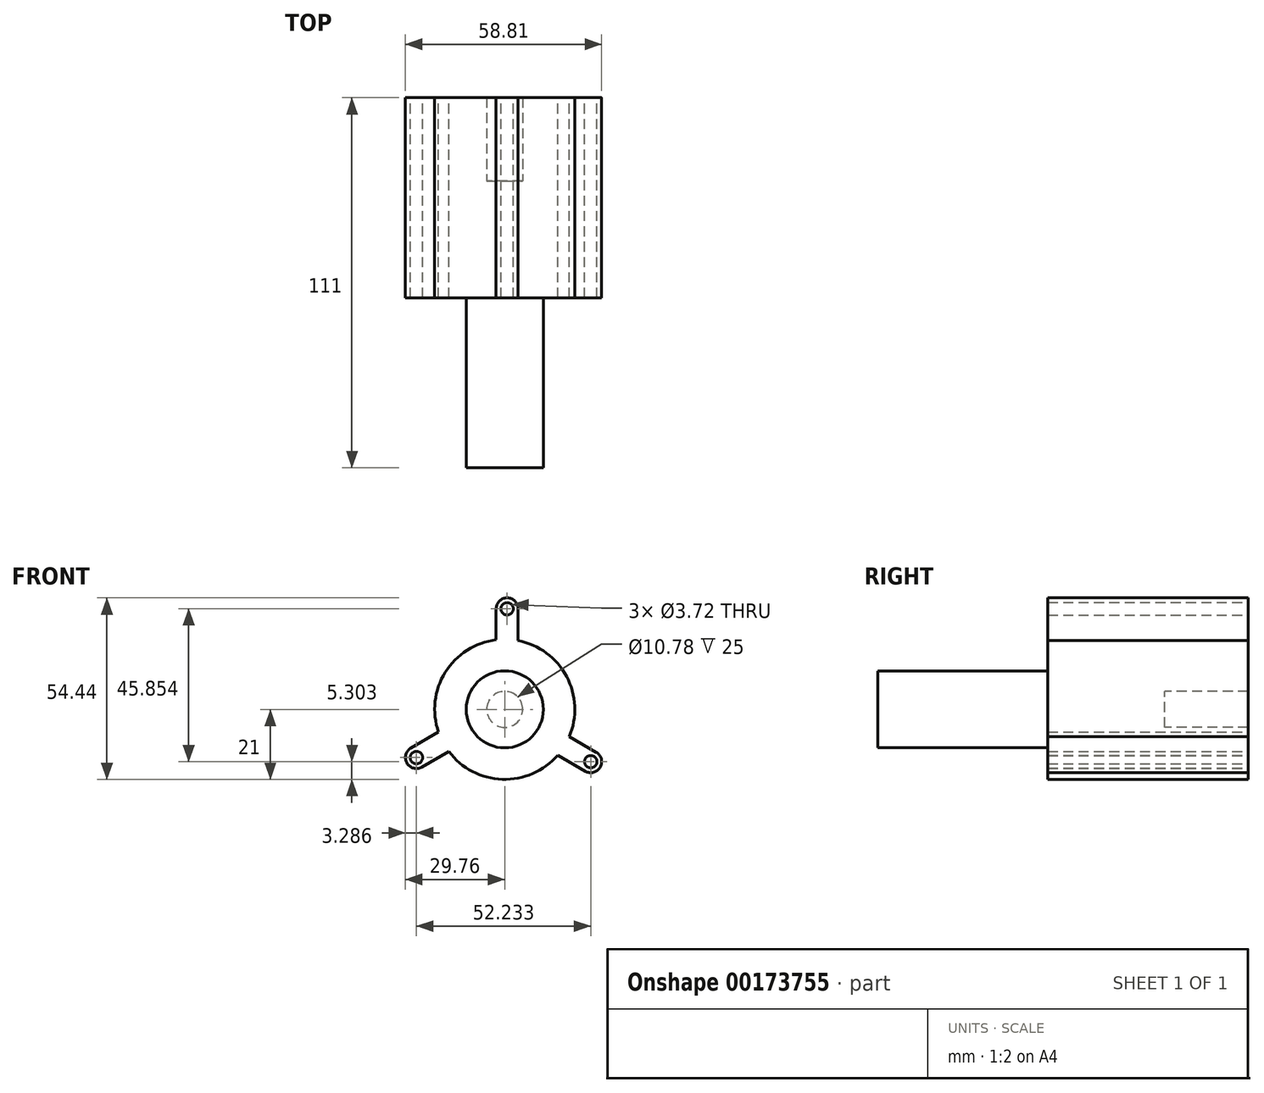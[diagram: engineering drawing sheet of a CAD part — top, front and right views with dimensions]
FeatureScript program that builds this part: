
annotation { "Feature Type Name" : "Feature", "Feature Type Description" : "" }
export const myFeature = defineFeature(function(context is Context, id is Id, definition is map)
    precondition{}
    {
        {
            var Q0;
            Q0=qCreatedBy(makeId("Front.planeOp"),FACE);
            var sketch = newSketch(context, id + "F0", { "sketchPlane" : qUnion([Q0])});
            skCircle(sketch, "E0", {"center": v(0, 0) * mm, "radius": 21 * mm});
            skLineSegment(sketch, "E1.left", {"start": v(-2.57, 30.16) * mm, "end": v(-2.57, 15) * mm});
            skLineSegment(sketch, "E1.right", {"start": v(4, 30.16) * mm, "end": v(4, 15) * mm});
            skArc(sketch, "E2", {"start": v(4, 30.16) * mm, "mid": v(0.71, 33.44) * mm, "end": v(-2.57, 30.16) * mm});
            skCircle(sketch, "E3", {"center": v(0.71, 30.16) * mm, "radius": 1.86 * mm});
            skLineSegment(sketch, "E4.1.0", {"start": v(24.12, -18.54) * mm, "end": v(11, -10.97) * mm});
            skLineSegment(sketch, "E4.1.1", {"start": v(27.4, -12.85) * mm, "end": v(14.28, -5.28) * mm});
            skArc(sketch, "E4.1.2", {"start": v(24.12, -18.54) * mm, "mid": v(28.6, -17.34) * mm, "end": v(27.4, -12.85) * mm});
            skCircle(sketch, "E4.1.3", {"center": v(25.76, -15.7) * mm, "radius": 1.86 * mm});
            skLineSegment(sketch, "E4.2.0", {"start": v(-28.12, -11.61) * mm, "end": v(-15, -4.04) * mm});
            skLineSegment(sketch, "E4.2.1", {"start": v(-24.83, -17.3) * mm, "end": v(-11.7, -9.73) * mm});
            skArc(sketch, "E4.2.2", {"start": v(-28.12, -11.61) * mm, "mid": v(-29.32, -16.1) * mm, "end": v(-24.83, -17.3) * mm});
            skCircle(sketch, "E4.2.3", {"center": v(-26.47, -14.46) * mm, "radius": 1.86 * mm});
            skLineSegment(sketch, "E4.anchor1", {"start": v(0, 0) * mm, "end": v(4, 15) * mm, "construction": true});
            skLineSegment(sketch, "E4.anchor2", {"start": v(0, 0) * mm, "end": v(-15, -4.04) * mm, "construction": true});
            skSolve(sketch);
        }
        {
            var Q0;
            {var subQ0=sQuery(id+"F0.wireOp",EDGE,"E0");var subQ4=makeQuery(id+"F0.imprint","INTERSECT",VERTEX,{"derivedFrom":[subQ0,sQuery(id+"F0.wireOp",EDGE,"E1.left")]});Q0=makeQuery(id+"F0.imprint","IMPRINT",FACE,{"disambiguationData":[TD([[makeQuery(id+"F0.imprint","IMPRINT",EDGE,{"disambiguationData":[TD([[subQ4,1.0]])],"derivedFrom":subQ0}),1.0]])]});}
            var Q1;
            {var subQ0=sQuery(id+"F0.wireOp",EDGE,"E2");Q1=makeQuery(id+"F0.imprint","IMPRINT",FACE,{"disambiguationData":[TD([[makeQuery(id+"F0.imprint","IMPRINT",EDGE,{"derivedFrom":subQ0}),1.0]])]});}
            var Q2;
            {var subQ0=sQuery(id+"F0.wireOp",EDGE,"E2");Q2=makeQuery(id+"F0.imprint","IMPRINT",FACE,{"disambiguationData":[TD([[makeQuery(id+"F0.imprint","IMPRINT",EDGE,{"derivedFrom":subQ0}),1.0]])]});}
            var Q3;
            {var subQ0=sQuery(id+"F0.wireOp",EDGE,"E4.2.2");Q3=makeQuery(id+"F0.imprint","IMPRINT",FACE,{"disambiguationData":[TD([[makeQuery(id+"F0.imprint","IMPRINT",EDGE,{"derivedFrom":subQ0}),1.0]])]});}
            var Q4;
            {var subQ0=sQuery(id+"F0.wireOp",EDGE,"E4.1.2");Q4=makeQuery(id+"F0.imprint","IMPRINT",FACE,{"disambiguationData":[TD([[makeQuery(id+"F0.imprint","IMPRINT",EDGE,{"derivedFrom":subQ0}),1.0]])]});}
            extrude(context, id + "F1", {"entities" : qUnion([Q0, Q1, Q2, Q3, Q4]), "depth" : 25 * mm});
        }
        {
            var Q0;
            Q0=makeQuery(id+"F1.opExtrude","CAP_FACE",FACE,{"disambiguationData":[OSD([sQuery(id+"F0.wireOp",EDGE,"E0"),sQuery(id+"F0.wireOp",EDGE,"E1.left"),sQuery(id+"F0.wireOp",EDGE,"E1.right"),sQuery(id+"F0.wireOp",EDGE,"E2"),sQuery(id+"F0.wireOp",EDGE,"E3"),sQuery(id+"F0.wireOp",EDGE,"E4.1.0"),sQuery(id+"F0.wireOp",EDGE,"E4.1.1"),sQuery(id+"F0.wireOp",EDGE,"E4.1.2"),sQuery(id+"F0.wireOp",EDGE,"E4.1.3"),sQuery(id+"F0.wireOp",EDGE,"E4.2.0"),sQuery(id+"F0.wireOp",EDGE,"E4.2.1"),sQuery(id+"F0.wireOp",EDGE,"E4.2.2"),sQuery(id+"F0.wireOp",EDGE,"E4.2.3")])],"isStart":true});
            var Q1;
            Q1=makeQuery(id+"F1.opExtrude","CAP_FACE",FACE,{"disambiguationData":[OSD([sQuery(id+"F0.wireOp",EDGE,"E0"),sQuery(id+"F0.wireOp",EDGE,"E1.left"),sQuery(id+"F0.wireOp",EDGE,"E1.right"),sQuery(id+"F0.wireOp",EDGE,"E2"),sQuery(id+"F0.wireOp",EDGE,"E3"),sQuery(id+"F0.wireOp",EDGE,"E4.1.0"),sQuery(id+"F0.wireOp",EDGE,"E4.1.1"),sQuery(id+"F0.wireOp",EDGE,"E4.1.2"),sQuery(id+"F0.wireOp",EDGE,"E4.1.3"),sQuery(id+"F0.wireOp",EDGE,"E4.2.0"),sQuery(id+"F0.wireOp",EDGE,"E4.2.1"),sQuery(id+"F0.wireOp",EDGE,"E4.2.2"),sQuery(id+"F0.wireOp",EDGE,"E4.2.3")])],"isStart":false});
            extrude(context, id + "F2", {"entities" : qUnion([Q0, Q1]), "operationType" : NewBodyOperationType.ADD, "depth" : 25 * mm});
        }
        {
            var Q0;
            Q0=qCreatedBy(makeId("Front.planeOp"),FACE);
            var sketch = newSketch(context, id + "F3", { "sketchPlane" : qUnion([Q0])});
            skCircle(sketch, "E5", {"center": v(0, 0) * mm, "radius": 11.54 * mm});
            skSolve(sketch);
        }
        {
            var Q0;
            Q0 = qSketchRegion(id + "F3", true);
            extrude(context, id + "F4", {"entities" : qUnion([Q0]), "operationType" : NewBodyOperationType.ADD, "depth" : 80 * mm});
        }
        {
            var Q0;
            Q0=makeQuery(id+"F4.opExtrude","CAP_FACE",FACE,{"disambiguationData":[OSD([sQuery(id+"F3.wireOp",EDGE,"E5")])],"isStart":false});
            var Q1;
            Q1=makeQuery(id+"F1.opExtrude","CAP_FACE",FACE,{"disambiguationData":[OSD([sQuery(id+"F0.wireOp",EDGE,"E0"),sQuery(id+"F0.wireOp",EDGE,"E1.left"),sQuery(id+"F0.wireOp",EDGE,"E1.right"),sQuery(id+"F0.wireOp",EDGE,"E2"),sQuery(id+"F0.wireOp",EDGE,"E3"),sQuery(id+"F0.wireOp",EDGE,"E4.1.0"),sQuery(id+"F0.wireOp",EDGE,"E4.1.1"),sQuery(id+"F0.wireOp",EDGE,"E4.1.2"),sQuery(id+"F0.wireOp",EDGE,"E4.1.3"),sQuery(id+"F0.wireOp",EDGE,"E4.2.0"),sQuery(id+"F0.wireOp",EDGE,"E4.2.1"),sQuery(id+"F0.wireOp",EDGE,"E4.2.2"),sQuery(id+"F0.wireOp",EDGE,"E4.2.3")])],"isStart":false});
            extrude(context, id + "F5", {"entities" : qUnion([Q0, Q1]), "operationType" : NewBodyOperationType.ADD, "depth" : 3 * mm});
        }
        {
            var Q0;
            Q0=makeQuery(id+"F5.opExtrude","CAP_FACE",FACE,{"disambiguationData":[OSD([sQuery(id+"F0.wireOp",EDGE,"E0"),sQuery(id+"F0.wireOp",EDGE,"E1.left"),sQuery(id+"F0.wireOp",EDGE,"E1.right"),sQuery(id+"F0.wireOp",EDGE,"E2"),sQuery(id+"F0.wireOp",EDGE,"E3"),sQuery(id+"F0.wireOp",EDGE,"E4.1.0"),sQuery(id+"F0.wireOp",EDGE,"E4.1.1"),sQuery(id+"F0.wireOp",EDGE,"E4.1.2"),sQuery(id+"F0.wireOp",EDGE,"E4.1.3"),sQuery(id+"F0.wireOp",EDGE,"E4.2.0"),sQuery(id+"F0.wireOp",EDGE,"E4.2.1"),sQuery(id+"F0.wireOp",EDGE,"E4.2.2"),sQuery(id+"F0.wireOp",EDGE,"E4.2.3")])],"isStart":false});
            extrude(context, id + "F6", {"entities" : qUnion([Q0]), "operationType" : NewBodyOperationType.ADD, "depth" : 3 * mm});
        }
        {
            var Q0;
            Q0=qCreatedBy(makeId("Front.planeOp"),FACE);
            var sketch = newSketch(context, id + "F7", { "sketchPlane" : qUnion([Q0])});
            skCircle(sketch, "E6", {"center": v(0, 0) * mm, "radius": 5.39 * mm});
            skSolve(sketch);
        }
        {
            var Q0;
            Q0 = qSketchRegion(id + "F7", true);
            extrude(context, id + "F8", {"entities" : qUnion([Q0]), "operationType" : NewBodyOperationType.REMOVE, "endBound" : BoundingType.THROUGH_ALL, "oppositeDirection" : true, "depth" : 20 * mm});
        }
        {
            var Q0;
            Q0=makeQuery(id+"F6.opExtrude","CAP_FACE",FACE,{"disambiguationData":[OSD([sQuery(id+"F0.wireOp",EDGE,"E0"),sQuery(id+"F0.wireOp",EDGE,"E1.left"),sQuery(id+"F0.wireOp",EDGE,"E1.right"),sQuery(id+"F0.wireOp",EDGE,"E2"),sQuery(id+"F0.wireOp",EDGE,"E3"),sQuery(id+"F0.wireOp",EDGE,"E4.1.0"),sQuery(id+"F0.wireOp",EDGE,"E4.1.1"),sQuery(id+"F0.wireOp",EDGE,"E4.1.2"),sQuery(id+"F0.wireOp",EDGE,"E4.1.3"),sQuery(id+"F0.wireOp",EDGE,"E4.2.0"),sQuery(id+"F0.wireOp",EDGE,"E4.2.1"),sQuery(id+"F0.wireOp",EDGE,"E4.2.2"),sQuery(id+"F0.wireOp",EDGE,"E4.2.3")])],"isStart":false});
            extrude(context, id + "F9", {"entities" : qUnion([Q0]), "operationType" : NewBodyOperationType.ADD, "depth" : 3 * mm});
        }
        {
            var Q0;
            Q0=makeQuery(id+"F9.opExtrude","CAP_FACE",FACE,{"disambiguationData":[OSD([sQuery(id+"F0.wireOp",EDGE,"E0"),sQuery(id+"F0.wireOp",EDGE,"E1.left"),sQuery(id+"F0.wireOp",EDGE,"E1.right"),sQuery(id+"F0.wireOp",EDGE,"E2"),sQuery(id+"F0.wireOp",EDGE,"E3"),sQuery(id+"F0.wireOp",EDGE,"E4.1.0"),sQuery(id+"F0.wireOp",EDGE,"E4.1.1"),sQuery(id+"F0.wireOp",EDGE,"E4.1.2"),sQuery(id+"F0.wireOp",EDGE,"E4.1.3"),sQuery(id+"F0.wireOp",EDGE,"E4.2.0"),sQuery(id+"F0.wireOp",EDGE,"E4.2.1"),sQuery(id+"F0.wireOp",EDGE,"E4.2.2"),sQuery(id+"F0.wireOp",EDGE,"E4.2.3")])],"isStart":false});
            extrude(context, id + "F10", {"entities" : qUnion([Q0]), "operationType" : NewBodyOperationType.ADD, "depth" : 1 * mm});
        }
        {
            var Q0;
            Q0=makeQuery(id+"F5.opExtrude","CAP_FACE",FACE,{"disambiguationData":[OSD([sQuery(id+"F3.wireOp",EDGE,"E5")])],"isStart":false});
            extrude(context, id + "F11", {"entities" : qUnion([Q0]), "operationType" : NewBodyOperationType.ADD, "depth" : 3 * mm});
        }
    });
